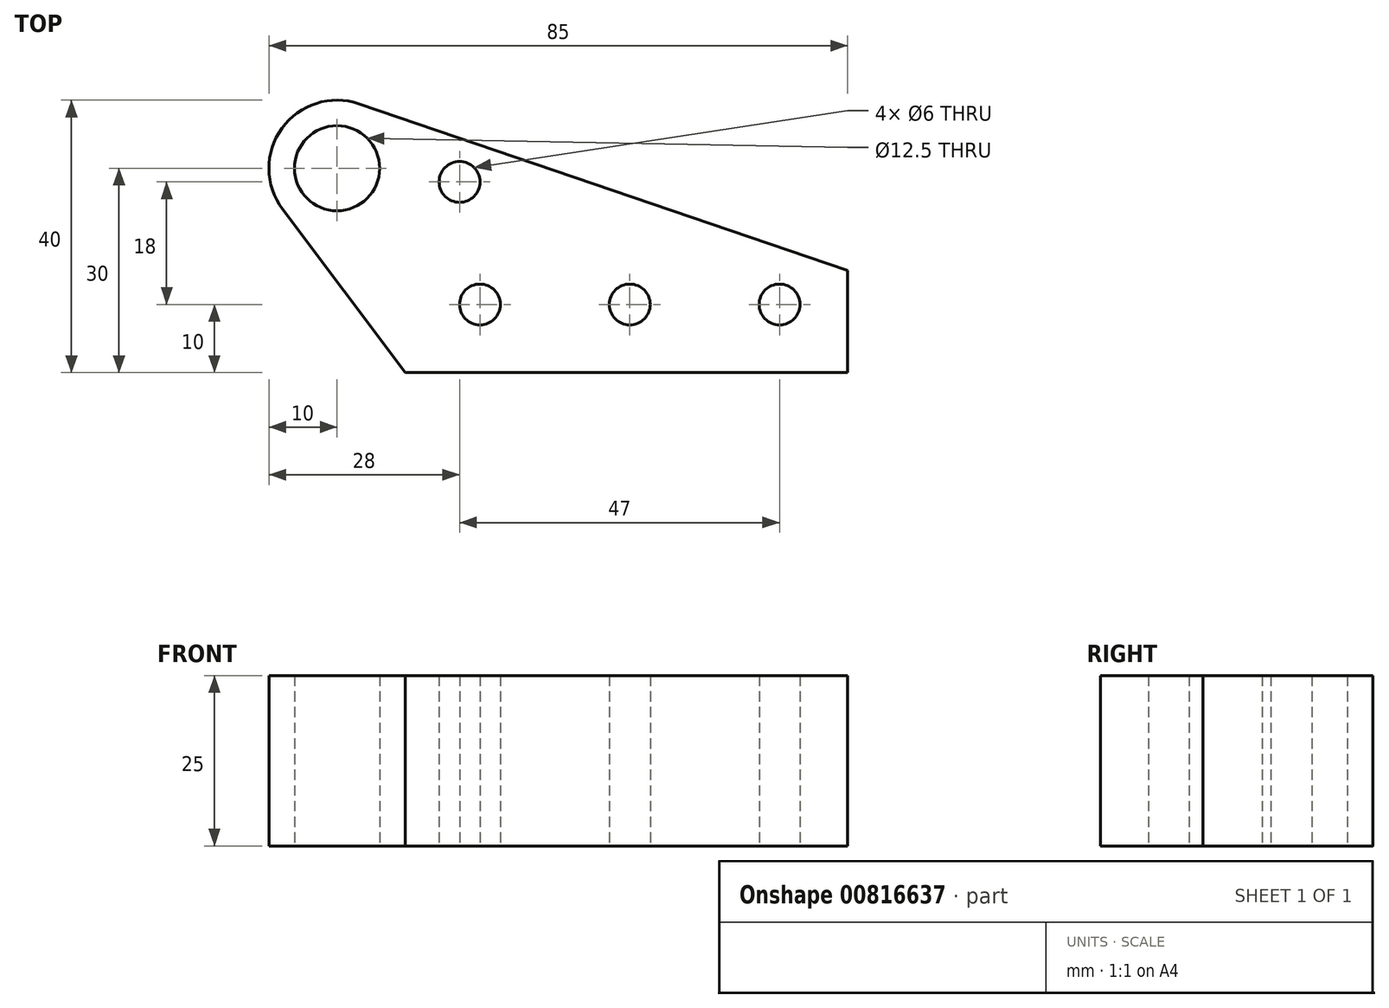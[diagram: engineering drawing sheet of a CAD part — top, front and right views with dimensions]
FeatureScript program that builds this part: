
annotation { "Feature Type Name" : "Feature", "Feature Type Description" : "" }
export const myFeature = defineFeature(function(context is Context, id is Id, definition is map)
    precondition{}
    {
        {
            var Q0;
            Q0=qCreatedBy(makeId("Top.planeOp"),FACE);
            var sketch = newSketch(context, id + "F0", { "sketchPlane" : qUnion([Q0])});
            skArc(sketch, "E0", {"start": v(-34.77, 19.47) * mm, "mid": v(-46.1, 15.87) * mm, "end": v(-46, 4) * mm});
            skLineSegment(sketch, "E1.top", {"start": v(-28, -20) * mm, "end": v(37, -20) * mm});
            skLineSegment(sketch, "E1.right", {"start": v(37, -5) * mm, "end": v(37, -20) * mm});
            skLineSegment(sketch, "E2", {"start": v(-34.77, 19.47) * mm, "end": v(37, -5) * mm});
            skLineSegment(sketch, "E3", {"start": v(-46, 4) * mm, "end": v(-28, -20) * mm});
            skCircle(sketch, "E4", {"center": v(-38, 10) * mm, "radius": 6.25 * mm});
            skCircle(sketch, "E5", {"center": v(27, -10) * mm, "radius": 3 * mm});
            skCircle(sketch, "E6", {"center": v(5, -10) * mm, "radius": 3 * mm});
            skCircle(sketch, "E7", {"center": v(-17, -10) * mm, "radius": 3 * mm});
            skCircle(sketch, "E8", {"center": v(-20, 8) * mm, "radius": 3 * mm});
            skSolve(sketch);
        }
        {
            var Q0;
            Q0=makeQuery(id+"F0.imprint","IMPRINT",FACE,{"disambiguationData":[TD([[makeQuery(id+"F0.imprint","IMPRINT",EDGE,{"derivedFrom":sQuery(id+"F0.wireOp",EDGE,"E0")}),1.0]])]});
            extrude(context, id + "F1", {"entities" : qUnion([Q0]), "depth" : 25 * mm, "offsetDistance" : 25 * mm});
        }
    });
